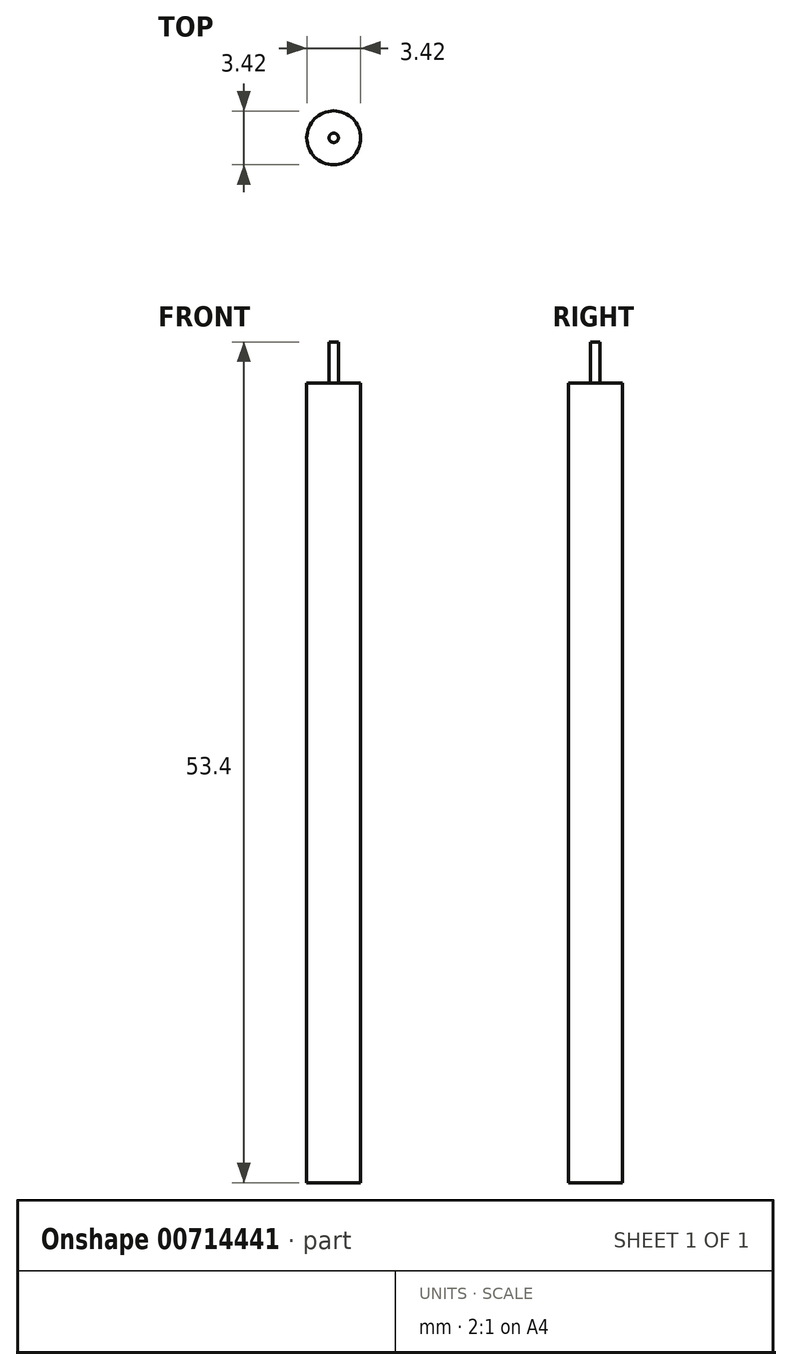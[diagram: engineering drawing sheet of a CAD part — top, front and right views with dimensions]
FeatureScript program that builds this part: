
annotation { "Feature Type Name" : "Feature", "Feature Type Description" : "" }
export const myFeature = defineFeature(function(context is Context, id is Id, definition is map)
    precondition{}
    {
        {
            var Q0;
            Q0=qCreatedBy(makeId("Top.planeOp"),FACE);
            var sketch = newSketch(context, id + "F0", { "sketchPlane" : qUnion([Q0])});
            skCircle(sketch, "E0", {"center": v(0, 0) * mm, "radius": 0.3 * mm});
            skSolve(sketch);
        }
        {
            var Q0;
            Q0=makeQuery(id+"F0.imprint","IMPRINT",FACE,{"disambiguationData":[TD([[makeQuery(id+"F0.imprint","IMPRINT",EDGE,{"derivedFrom":sQuery(id+"F0.wireOp",EDGE,"E0")}),1.0]])]});
            extrude(context, id + "F1", {"entities" : qUnion([Q0]), "oppositeDirection" : true, "depth" : 2.6 * mm});
        }
        {
            var Q0;
            Q0=makeQuery(id+"F1.opExtrude","CAP_FACE",FACE,{"disambiguationData":[OSD([sQuery(id+"F0.wireOp",EDGE,"E0")])],"isStart":false});
            var sketch = newSketch(context, id + "F2", { "sketchPlane" : qUnion([Q0])});
            skCircle(sketch, "E1", {"center": v(0, 0) * mm, "radius": 1.71 * mm});
            skSolve(sketch);
        }
        {
            var Q0;
            Q0=qSketchRegion(id+"F2",true);
            extrude(context, id + "F3", {"entities" : qUnion([Q0]), "operationType" : NewBodyOperationType.ADD, "depth" : 50.8 * mm});
        }
    });
